# Revit family: 106 - TUBO DE CONEXIÓN A MURO
name_source: partatom
category: Uniones de tubería
units: mm (PartAtom-declared; Revit-internal decimal feet)

## family parameters
Compartido = No
Corte con vacíos al cargar = No
Cota de conector redondo = Radio de uso
Número OmniClass = 23.45.05.14.21.11
Se basa en plano de trabajo = No
Siempre vertical = Sí
Tipo de pieza = Codo
Título OmniClass = Bath/Shower Units

## types (1)
- TUBO DE CONEXIÓN A MURO
    Bath Tub Material = <Por categoría>
    CWFU = 1
    Cold Water Radius = 8 mm
    Elevación por defecto = 0 cm
    F_Alto = 14.2 cm
    F_Ancho = 14.2 cm
    F_Color = Blanco
    F_Descripción = Tubo de conexión para inodoro multidescarga, para instalación muro. Fabricado en PVC de alta resistencia
    F_Peso = 0.43 kgf
    F_Profundidad = 31 cm
    F_SKU = SC0024610001BO
    F_Tipo de instalación = A muro
    Faucet Material = <Por categoría>
    HWFU = 1
    Sanitary Radius = 20 mm
    URL = https://www.fanaloza.cl
    WFU = 2

## geometry (parser evidence)
native form markers: Sweep x6
no freeform markers — native parametric forms only
